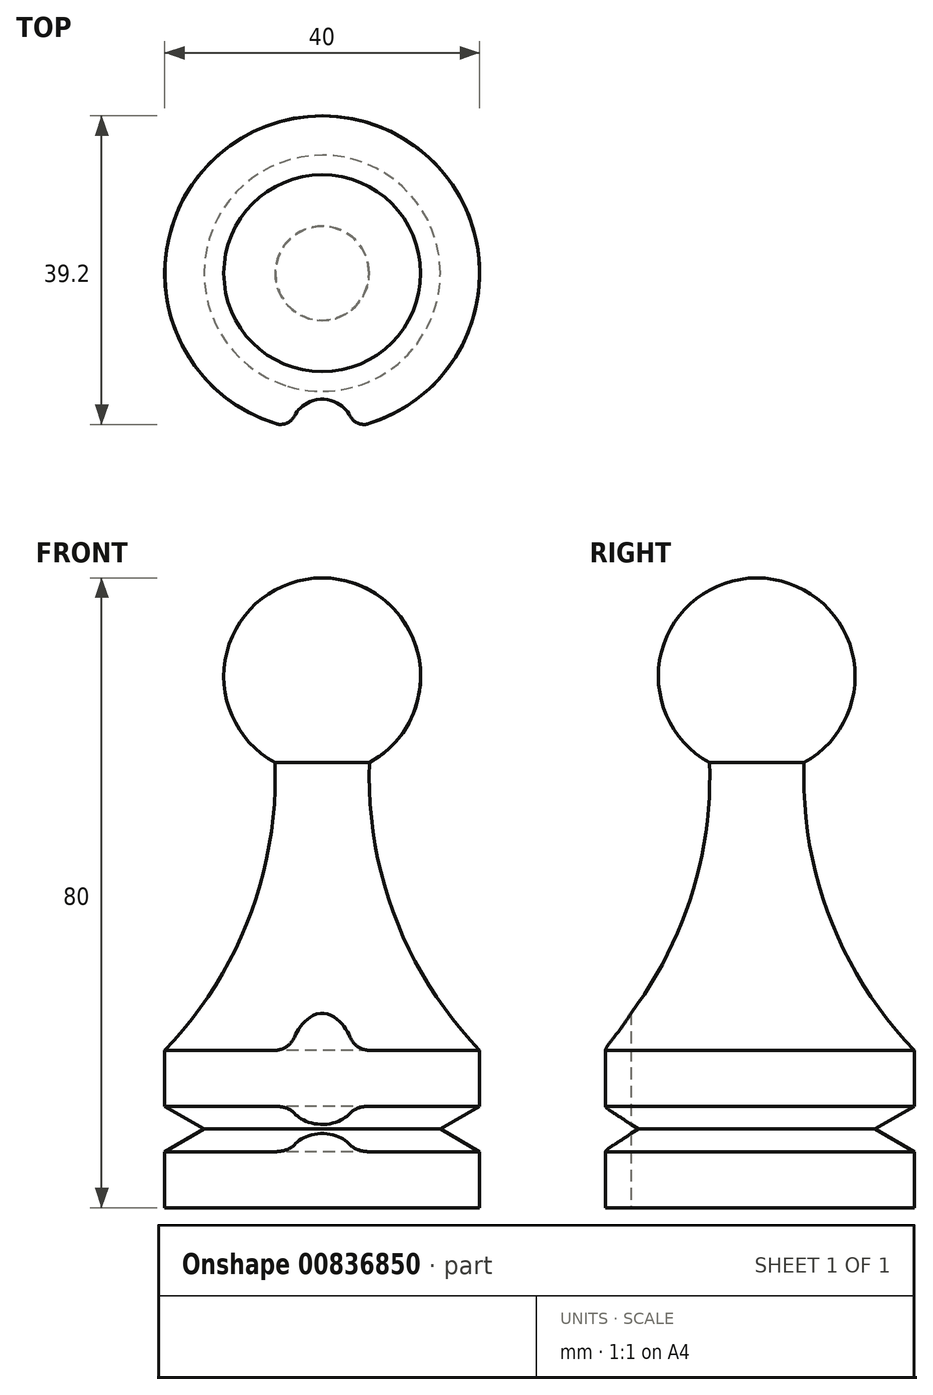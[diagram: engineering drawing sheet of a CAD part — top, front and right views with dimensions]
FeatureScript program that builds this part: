
annotation { "Feature Type Name" : "Feature", "Feature Type Description" : "" }
export const myFeature = defineFeature(function(context is Context, id is Id, definition is map)
    precondition{}
    {
        {
            var Q0;
            Q0=qCreatedBy(makeId("Front.planeOp"),FACE);
            var sketch = newSketch(context, id + "F0", { "sketchPlane" : qUnion([Q0])});
            skLineSegment(sketch, "E0", {"start": v(0, 85.51) * mm, "end": v(0, -118.16) * mm, "construction": true});
            skLineSegment(sketch, "E1", {"start": v(0, 0) * mm, "end": v(20, 0) * mm});
            skLineSegment(sketch, "E2", {"start": v(20, 0) * mm, "end": v(20, 7.11) * mm});
            skLineSegment(sketch, "E3", {"start": v(20, 12.89) * mm, "end": v(15, 10) * mm});
            skLineSegment(sketch, "E4", {"start": v(15, 10) * mm, "end": v(20, 7.11) * mm});
            skLineSegment(sketch, "E5", {"start": v(20, 12.89) * mm, "end": v(20, 20) * mm});
            skArc(sketch, "E6", {"start": v(6, 56.53) * mm, "mid": v(9.28, 36.84) * mm, "end": v(20, 20) * mm});
            skArc(sketch, "E7", {"start": v(6, 56.53) * mm, "mid": v(12.11, 70.6) * mm, "end": v(0, 80) * mm});
            skLineSegment(sketch, "E8", {"start": v(0, 80) * mm, "end": v(0, 0) * mm});
            skSolve(sketch);
        }
        {
            var Q0;
            Q0 = qSketchRegion(id + "F0", true);
            var Q1;
            Q1=sQuery(id+"F0.wireOp",EDGE,"E8");
            revolve(context, id + "F1", {"surfaceOperationType" : NewSurfaceOperationType.NEW, "entities" : qUnion([Q0]), "axis" : qUnion([Q1]), "revolveType" : RevolveType.FULL});
        }
        {
            var Q0;
            Q0=makeQuery(id+"F1.opRevolve","SWEPT_FACE",FACE,{"disambiguationData":[OSD([sQuery(id+"F0.wireOp",EDGE,"E1")])]});
            var sketch = newSketch(context, id + "F2", { "sketchPlane" : qUnion([Q0])});
            skCircle(sketch, "E9", {"center": v(0, 20) * mm, "radius": 4 * mm});
            skSolve(sketch);
        }
        {
            var Q0;
            Q0 = qSketchRegion(id + "F2", true);
            extrude(context, id + "F3", {"entities" : qUnion([Q0]), "operationType" : NewBodyOperationType.REMOVE, "endBound" : BoundingType.THROUGH_ALL, "oppositeDirection" : true, "depth" : 25 * mm, "offsetDistance" : 25 * mm});
        }
        {
            var Q0;
            Q0=makeQuery(id+"F3.boolean.opBoolean","INTERSECT",EDGE,{"disambiguationData":[OD(0.0)],"derivedFrom":[makeQuery(id+"F1.opRevolve","SWEPT_FACE",FACE,{"disambiguationData":[OSD([sQuery(id+"F0.wireOp",EDGE,"E5")])]}),makeQuery(id+"F3.opExtrude","SWEPT_FACE",FACE,{"disambiguationData":[OSD([sQuery(id+"F2.wireOp",EDGE,"E9")])]})]});
            var Q1;
            Q1=makeQuery(id+"F3.boolean.opBoolean","INTERSECT",EDGE,{"disambiguationData":[OD(0.0)],"derivedFrom":[makeQuery(id+"F1.opRevolve","SWEPT_FACE",FACE,{"disambiguationData":[OSD([sQuery(id+"F0.wireOp",EDGE,"E2")])]}),makeQuery(id+"F3.opExtrude","SWEPT_FACE",FACE,{"disambiguationData":[OSD([sQuery(id+"F2.wireOp",EDGE,"E9")])]})]});
            var Q2;
            Q2=makeQuery(id+"F3.boolean.opBoolean","INTERSECT",EDGE,{"disambiguationData":[OD(1.0)],"derivedFrom":[makeQuery(id+"F1.opRevolve","SWEPT_FACE",FACE,{"disambiguationData":[OSD([sQuery(id+"F0.wireOp",EDGE,"E5")])]}),makeQuery(id+"F3.opExtrude","SWEPT_FACE",FACE,{"disambiguationData":[OSD([sQuery(id+"F2.wireOp",EDGE,"E9")])]})]});
            var Q3;
            Q3=makeQuery(id+"F3.boolean.opBoolean","INTERSECT",EDGE,{"disambiguationData":[OD(1.0)],"derivedFrom":[makeQuery(id+"F1.opRevolve","SWEPT_FACE",FACE,{"disambiguationData":[OSD([sQuery(id+"F0.wireOp",EDGE,"E2")])]}),makeQuery(id+"F3.opExtrude","SWEPT_FACE",FACE,{"disambiguationData":[OSD([sQuery(id+"F2.wireOp",EDGE,"E9")])]})]});
            fillet(context, id + "F4", {"entities" : qUnion([Q0, Q1, Q2, Q3]), "radius" : 2 * mm, "tangentPropagation" : true, "allowEdgeOverflow" : false});
        }
    });
